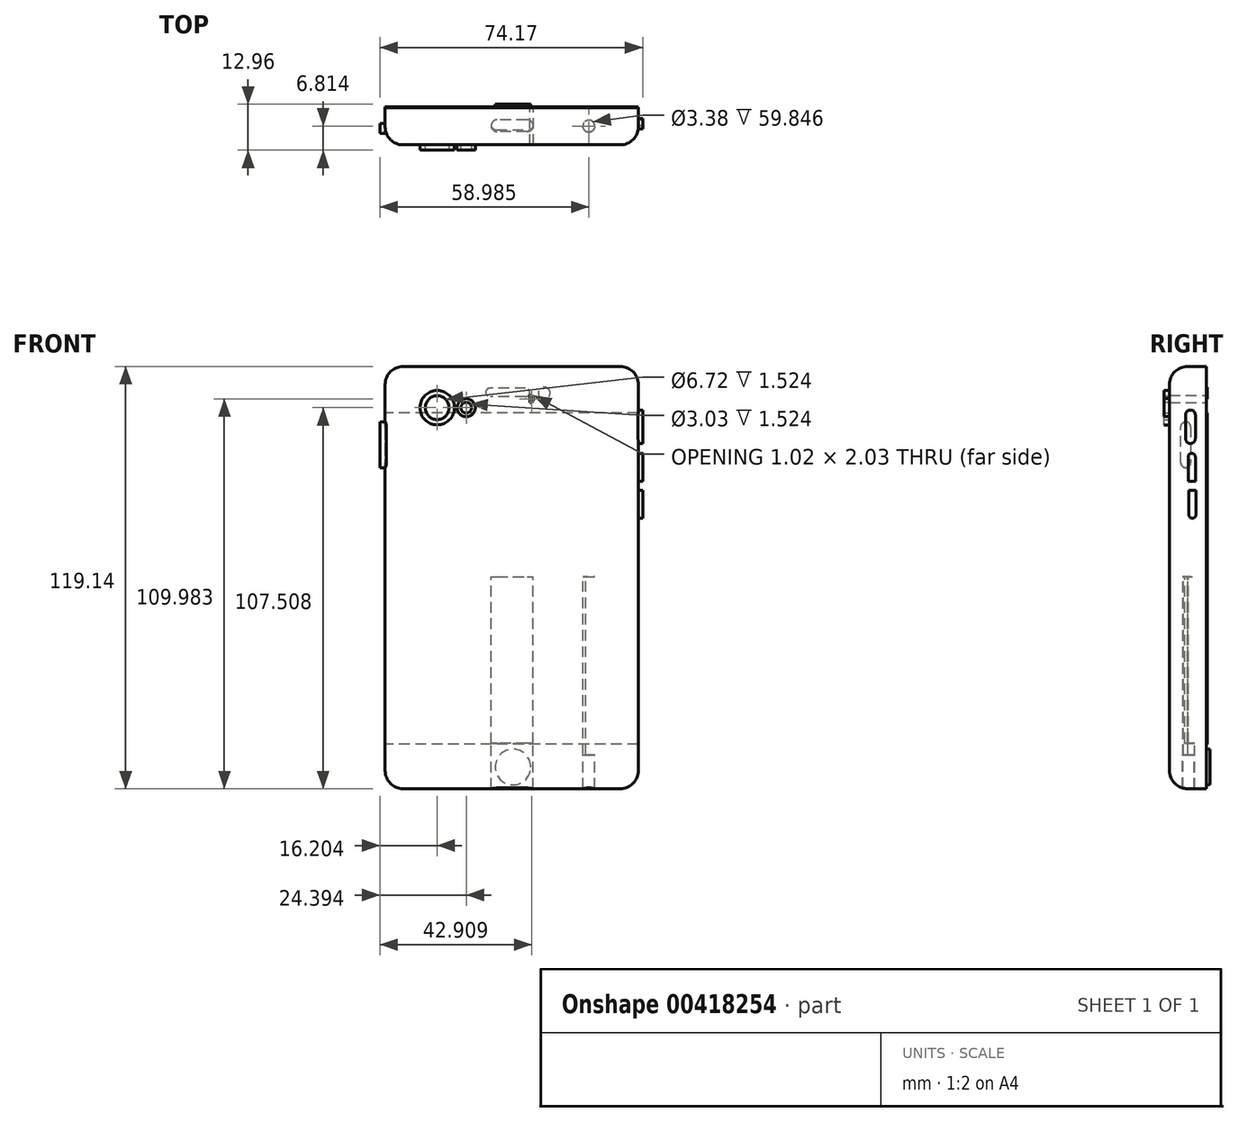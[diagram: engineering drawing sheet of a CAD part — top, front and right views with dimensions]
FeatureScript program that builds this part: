
annotation { "Feature Type Name" : "Feature", "Feature Type Description" : "" }
export const myFeature = defineFeature(function(context is Context, id is Id, definition is map)
    precondition{}
    {
        {
            var Q0;
            Q0=qCreatedBy(makeId("Front.planeOp"),FACE);
            var sketch = newSketch(context, id + "F0", { "sketchPlane" : qUnion([Q0])});
            skLineSegment(sketch, "E0.bottom", {"start": v(-32.74, 55.4) * mm, "end": v(31.45, 55.4) * mm});
            skLineSegment(sketch, "E0.top", {"start": v(-32.74, -55.78) * mm, "end": v(31.45, -55.78) * mm});
            skLineSegment(sketch, "E0.left", {"start": v(-32.74, 55.4) * mm, "end": v(-32.74, -55.78) * mm});
            skLineSegment(sketch, "E0.right", {"start": v(31.45, 55.4) * mm, "end": v(31.45, -55.78) * mm});
            skCircle(sketch, "E1", {"center": v(0, -48.2) * mm, "radius": 6.56 * mm});
            skLineSegment(sketch, "E2", {"start": v(-32.74, 43.75) * mm, "end": v(31.45, 43.75) * mm});
            skLineSegment(sketch, "E3.bottom", {"start": v(-4.25, 51.15) * mm, "end": v(4.8, 51.15) * mm});
            skLineSegment(sketch, "E3.top", {"start": v(-4.25, 49.12) * mm, "end": v(4.8, 49.12) * mm});
            skLineSegment(sketch, "E3.left", {"start": v(-4.25, 51.15) * mm, "end": v(-4.25, 49.12) * mm});
            skLineSegment(sketch, "E3.right", {"start": v(4.8, 51.15) * mm, "end": v(4.8, 49.12) * mm});
            skArc(sketch, "E4", {"start": v(4.8, 51.15) * mm, "mid": v(5.83, 50.13) * mm, "end": v(4.8, 49.12) * mm});
            skCircle(sketch, "E5", {"center": v(-8.7, 50.04) * mm, "radius": 1.1 * mm});
            skLineSegment(sketch, "E6.bottom", {"start": v(-36.07, 59.3) * mm, "end": v(35.33, 59.3) * mm});
            skLineSegment(sketch, "E6.top", {"start": v(-36.07, -59.85) * mm, "end": v(35.33, -59.85) * mm});
            skLineSegment(sketch, "E6.left", {"start": v(-36.07, 59.3) * mm, "end": v(-36.07, -59.85) * mm});
            skLineSegment(sketch, "E6.right", {"start": v(35.33, 59.3) * mm, "end": v(35.33, -59.85) * mm});
            skCircle(sketch, "E7", {"center": v(0, -48.2) * mm, "radius": 5.74 * mm});
            skCircle(sketch, "E8", {"center": v(-8.7, 50.04) * mm, "radius": 1.7 * mm});
            skSolve(sketch);
        }
        {
            var Q0;
            Q0 = qSketchRegion(id + "F0", true);
            var Q1;
            Q1=makeQuery(id+"F0.imprint","IMPRINT",FACE,{"disambiguationData":[TD([[makeQuery(id+"F0.imprint","IMPRINT",EDGE,{"derivedFrom":sQuery(id+"F0.wireOp",EDGE,"E7")}),1.0]])]});
            var Q2;
            Q2=makeQuery(id+"F0.imprint","IMPRINT",FACE,{"disambiguationData":[TD([[makeQuery(id+"F0.imprint","IMPRINT",EDGE,{"derivedFrom":sQuery(id+"F0.wireOp",EDGE,"E1")}),1.0]])]});
            var Q3;
            {var subQ1=sQuery(id+"F0.wireOp",EDGE,"E0.top");Q3=makeQuery(id+"F0.imprint","IMPRINT",FACE,{"disambiguationData":[TD([[makeQuery(id+"F0.imprint","IMPRINT",EDGE,{"derivedFrom":subQ1}),1.0]])]});}
            var Q4;
            Q4=makeQuery(id+"F0.imprint","IMPRINT",FACE,{"disambiguationData":[TD([[makeQuery(id+"F0.imprint","IMPRINT",EDGE,{"derivedFrom":sQuery(id+"F0.wireOp",EDGE,"E3.bottom")}),-1.0]])]});
            var Q5;
            Q5=makeQuery(id+"F0.imprint","IMPRINT",FACE,{"disambiguationData":[TD([[makeQuery(id+"F0.imprint","IMPRINT",EDGE,{"derivedFrom":sQuery(id+"F0.wireOp",EDGE,"E5")}),1.0]])]});
            var Q6;
            Q6=makeQuery(id+"F0.imprint","IMPRINT",FACE,{"disambiguationData":[TD([[makeQuery(id+"F0.imprint","IMPRINT",EDGE,{"derivedFrom":sQuery(id+"F0.wireOp",EDGE,"E4")}),-1.0]])]});
            var Q7;
            {var subQ1=sQuery(id+"F0.wireOp",EDGE,"E0.bottom");Q7=makeQuery(id+"F0.imprint","IMPRINT",FACE,{"disambiguationData":[TD([[makeQuery(id+"F0.imprint","IMPRINT",EDGE,{"derivedFrom":subQ1}),-1.0]])]});}
            var Q8;
            Q8=makeQuery(id+"F0.imprint","IMPRINT",FACE,{"disambiguationData":[TD([[makeQuery(id+"F0.imprint","IMPRINT",EDGE,{"derivedFrom":sQuery(id+"F0.wireOp",EDGE,"E5")}),-1.0]])]});
            extrude(context, id + "F1", {"entities" : qUnion([Q0, Q1, Q2, Q3, Q4, Q5, Q6, Q7, Q8]), "depth" : 10.4 * mm});
        }
        {
            var Q0;
            Q0=makeQuery(id+"F1.opExtrude","CAP_EDGE",EDGE,{"disambiguationData":[OSD([sQuery(id+"F0.wireOp",EDGE,"E6.bottom")])],"isStart":false});
            fillet(context, id + "F2", {"entities" : qUnion([Q0]), "radius" : 5.08 * mm, "tangentPropagation" : true, "allowEdgeOverflow" : false});
        }
        {
            var Q0;
            Q0=makeQuery(id+"F2.opFillet","BLEND_EDGE",EDGE,{"blendedFrom":[makeQuery(id+"F1.opExtrude","CAP_EDGE",EDGE,{"disambiguationData":[OSD([sQuery(id+"F0.wireOp",EDGE,"E6.bottom")])],"isStart":false}),makeQuery(id+"F1.opExtrude","SWEPT_FACE",FACE,{"disambiguationData":[OSD([sQuery(id+"F0.wireOp",EDGE,"E6.left")])]})],"blendedInto":[makeQuery(id+"F1.opExtrude","SWEPT_FACE",FACE,{"disambiguationData":[OSD([sQuery(id+"F0.wireOp",EDGE,"E6.left")])]})]});
            var Q1;
            Q1=makeQuery(id+"F2.opFillet","BLEND_EDGE",EDGE,{"blendedFrom":[makeQuery(id+"F1.opExtrude","CAP_EDGE",EDGE,{"disambiguationData":[OSD([sQuery(id+"F0.wireOp",EDGE,"E6.bottom")])],"isStart":false}),makeQuery(id+"F1.opExtrude","SWEPT_FACE",FACE,{"disambiguationData":[OSD([sQuery(id+"F0.wireOp",EDGE,"E6.right")])]})],"blendedInto":[makeQuery(id+"F1.opExtrude","SWEPT_FACE",FACE,{"disambiguationData":[OSD([sQuery(id+"F0.wireOp",EDGE,"E6.right")])]})]});
            var Q2;
            Q2=makeQuery(id+"F1.opExtrude","CAP_EDGE",EDGE,{"disambiguationData":[OSD([sQuery(id+"F0.wireOp",EDGE,"E6.left")])],"isStart":false});
            fillet(context, id + "F3", {"entities" : qUnion([Q0, Q1, Q2]), "radius" : 5.08 * mm, "tangentPropagation" : true, "allowEdgeOverflow" : false});
        }
        {
            var Q0;
            Q0=makeQuery(id+"F3.opFillet","BLEND_EDGE",EDGE,{"blendedFrom":[makeQuery(id+"F1.opExtrude","CAP_EDGE",EDGE,{"disambiguationData":[OSD([sQuery(id+"F0.wireOp",EDGE,"E6.left")])],"isStart":false}),makeQuery(id+"F1.opExtrude","SWEPT_FACE",FACE,{"disambiguationData":[OSD([sQuery(id+"F0.wireOp",EDGE,"E6.top")])]})],"blendedInto":[makeQuery(id+"F1.opExtrude","SWEPT_FACE",FACE,{"disambiguationData":[OSD([sQuery(id+"F0.wireOp",EDGE,"E6.top")])]})]});
            fillet(context, id + "F4", {"entities" : qUnion([Q0]), "radius" : 5.08 * mm, "tangentPropagation" : true, "allowEdgeOverflow" : false});
        }
        {
            var Q0;
            Q0=makeQuery(id+"F1.opExtrude","CAP_FACE",FACE,{"disambiguationData":[OSD([sQuery(id+"F0.wireOp",EDGE,"E6.bottom"),sQuery(id+"F0.wireOp",EDGE,"E6.top"),sQuery(id+"F0.wireOp",EDGE,"E6.left"),sQuery(id+"F0.wireOp",EDGE,"E6.right")])],"isStart":false});
            var sketch = newSketch(context, id + "F5", { "sketchPlane" : qUnion([Q0])});
            skCircle(sketch, "E9", {"center": v(-21.39, 47.66) * mm, "radius": 3.36 * mm});
            skCircle(sketch, "E10", {"center": v(-21.39, 47.66) * mm, "radius": 4.86 * mm});
            skCircle(sketch, "E11", {"center": v(-13.2, 47.66) * mm, "radius": 1.52 * mm});
            skCircle(sketch, "E12", {"center": v(-13.2, 47.66) * mm, "radius": 2.55 * mm});
            skSolve(sketch);
        }
        {
            var Q0;
            Q0=qCreatedBy(makeId("Right.planeOp"),FACE);
            var sketch = newSketch(context, id + "F6", { "sketchPlane" : qUnion([Q0])});
            skLineSegment(sketch, "E13.bottom", {"start": v(-5.92, 45.6) * mm, "end": v(-3.14, 45.6) * mm});
            skLineSegment(sketch, "E13.top", {"start": v(-5.92, 38.94) * mm, "end": v(-3.14, 38.94) * mm});
            skLineSegment(sketch, "E13.left", {"start": v(-5.92, 45.6) * mm, "end": v(-5.92, 38.94) * mm});
            skLineSegment(sketch, "E13.right", {"start": v(-3.14, 45.6) * mm, "end": v(-3.14, 38.94) * mm});
            skLineSegment(sketch, "E14.bottom", {"start": v(-5.18, 33.76) * mm, "end": v(-3.14, 33.76) * mm});
            skLineSegment(sketch, "E14.top", {"start": v(-5.18, 26.92) * mm, "end": v(-3.14, 26.92) * mm});
            skLineSegment(sketch, "E14.left", {"start": v(-5.18, 33.76) * mm, "end": v(-5.18, 26.92) * mm});
            skLineSegment(sketch, "E14.right", {"start": v(-3.14, 33.76) * mm, "end": v(-3.14, 26.92) * mm});
            skLineSegment(sketch, "E15.bottom", {"start": v(-5, 24.33) * mm, "end": v(-2.96, 24.33) * mm});
            skLineSegment(sketch, "E15.top", {"start": v(-5, 17.48) * mm, "end": v(-2.96, 17.48) * mm});
            skLineSegment(sketch, "E15.left", {"start": v(-5, 24.33) * mm, "end": v(-5, 17.48) * mm});
            skLineSegment(sketch, "E15.right", {"start": v(-2.96, 24.33) * mm, "end": v(-2.96, 17.48) * mm});
            skArc(sketch, "E16", {"start": v(-5.92, 45.6) * mm, "mid": v(-4.53, 46.99) * mm, "end": v(-3.14, 45.6) * mm});
            skArc(sketch, "E17", {"start": v(-5.92, 38.94) * mm, "mid": v(-4.53, 37.55) * mm, "end": v(-3.14, 38.94) * mm});
            skArc(sketch, "E18", {"start": v(-5.18, 33.76) * mm, "mid": v(-4.16, 34.78) * mm, "end": v(-3.14, 33.76) * mm});
            skArc(sketch, "E19", {"start": v(-5, 17.48) * mm, "mid": v(-3.98, 16.46) * mm, "end": v(-2.96, 17.48) * mm});
            skSolve(sketch);
        }
        {
            var Q0;
            Q0 = qSketchRegion(id + "F6", true);
            extrude(context, id + "F7", {"entities" : qUnion([Q0]), "operationType" : NewBodyOperationType.ADD, "depth" : 36.58 * mm});
        }
        {
            var Q0;
            Q0=qCreatedBy(makeId("Right.planeOp"),FACE);
            var sketch = newSketch(context, id + "F8", { "sketchPlane" : qUnion([Q0])});
            skLineSegment(sketch, "E20.bottom", {"start": v(-4.44, 42.27) * mm, "end": v(-7.21, 42.27) * mm});
            skLineSegment(sketch, "E20.top", {"start": v(-4.44, 32.1) * mm, "end": v(-7.21, 32.1) * mm});
            skLineSegment(sketch, "E20.left", {"start": v(-4.44, 42.27) * mm, "end": v(-4.44, 32.1) * mm});
            skLineSegment(sketch, "E20.right", {"start": v(-7.21, 42.27) * mm, "end": v(-7.21, 32.1) * mm});
            skArc(sketch, "E21", {"start": v(-7.21, 32.1) * mm, "mid": v(-5.83, 30.7) * mm, "end": v(-4.44, 32.1) * mm});
            skArc(sketch, "E22", {"start": v(-4.44, 42.27) * mm, "mid": v(-5.83, 43.66) * mm, "end": v(-7.21, 42.27) * mm});
            skSolve(sketch);
        }
        {
            var Q0;
            Q0 = qSketchRegion(id + "F8", true);
            extrude(context, id + "F9", {"entities" : qUnion([Q0]), "operationType" : NewBodyOperationType.ADD, "oppositeDirection" : true, "depth" : 37.6 * mm});
        }
        {
            var Q0;
            Q0 = qSketchRegion(id + "F5", true);
            extrude(context, id + "F10", {"entities" : qUnion([Q0]), "operationType" : NewBodyOperationType.ADD, "depth" : 1.52 * mm});
        }
        {
            var Q0;
            Q0=qCreatedBy(makeId("Front.planeOp"),FACE);
            var sketch = newSketch(context, id + "F11", { "sketchPlane" : qUnion([Q0])});
            skCircle(sketch, "E23", {"center": v(0, -53.74) * mm, "radius": 5.03 * mm});
            skSolve(sketch);
        }
        {
            var Q0;
            Q0 = qSketchRegion(id + "F11", true);
            extrude(context, id + "F12", {"entities" : qUnion([Q0]), "operationType" : NewBodyOperationType.ADD, "oppositeDirection" : true, "depth" : 1.02 * mm});
        }
        {
            var Q0;
            Q0=qCreatedBy(makeId("Front.planeOp"),FACE);
            var sketch = newSketch(context, id + "F13", { "sketchPlane" : qUnion([Q0])});
            skLineSegment(sketch, "E24.bottom", {"start": v(35.27, 46.19) * mm, "end": v(-36.07, 46.19) * mm});
            skLineSegment(sketch, "E24.top", {"start": v(35.27, -47.25) * mm, "end": v(-36.07, -47.25) * mm});
            skLineSegment(sketch, "E24.left", {"start": v(35.27, 46.19) * mm, "end": v(35.27, -47.25) * mm});
            skLineSegment(sketch, "E24.right", {"start": v(-36.07, 46.19) * mm, "end": v(-36.07, -47.25) * mm});
            skSolve(sketch);
        }
        {
            var Q0;
            Q0 = qSketchRegion(id + "F13", true);
            extrude(context, id + "F14", {"entities" : qUnion([Q0]), "operationType" : NewBodyOperationType.ADD, "oppositeDirection" : true, "depth" : 0.25 * mm});
        }
        {
            var Q0;
            Q0=qCreatedBy(makeId("Front.planeOp"),FACE);
            var sketch = newSketch(context, id + "F15", { "sketchPlane" : qUnion([Q0])});
            skLineSegment(sketch, "E25.bottom", {"start": v(3.51, 53.19) * mm, "end": v(-6.47, 53.19) * mm});
            skLineSegment(sketch, "E25.top", {"start": v(3.51, 50.78) * mm, "end": v(-6.47, 50.78) * mm});
            skLineSegment(sketch, "E25.left", {"start": v(3.51, 53.19) * mm, "end": v(3.51, 50.78) * mm});
            skLineSegment(sketch, "E25.right", {"start": v(-6.47, 53.19) * mm, "end": v(-6.47, 50.78) * mm});
            skArc(sketch, "E26", {"start": v(3.51, 50.78) * mm, "mid": v(4.72, 51.98) * mm, "end": v(3.51, 53.19) * mm});
            skArc(sketch, "E27", {"start": v(-6.47, 53.19) * mm, "mid": v(-7.68, 51.98) * mm, "end": v(-6.47, 50.78) * mm});
            skSolve(sketch);
        }
        {
            var Q0;
            Q0 = qSketchRegion(id + "F15", true);
            extrude(context, id + "F16", {"entities" : qUnion([Q0]), "operationType" : NewBodyOperationType.ADD, "oppositeDirection" : true, "depth" : 0.25 * mm});
        }
        {
            var Q0;
            Q0=qCreatedBy(makeId("Front.planeOp"),FACE);
            var sketch = newSketch(context, id + "F17", { "sketchPlane" : qUnion([Q0])});
            skCircle(sketch, "E28", {"center": v(8.81, 51.8) * mm, "radius": 1.66 * mm});
            skSolve(sketch);
        }
        {
            var Q0;
            Q0 = qSketchRegion(id + "F17", true);
            extrude(context, id + "F18", {"entities" : qUnion([Q0]), "operationType" : NewBodyOperationType.ADD, "oppositeDirection" : true, "depth" : 0.25 * mm});
        }
        {
            var Q0;
            Q0=qCreatedBy(makeId("Top.planeOp"),FACE);
            var sketch = newSketch(context, id + "F19", { "sketchPlane" : qUnion([Q0])});
            skLineSegment(sketch, "E29.bottom", {"start": v(-4.46, -6.69) * mm, "end": v(4.01, -6.69) * mm});
            skLineSegment(sketch, "E29.top", {"start": v(-4.46, -3.34) * mm, "end": v(4.01, -3.34) * mm});
            skLineSegment(sketch, "E29.left", {"start": v(-4.46, -6.69) * mm, "end": v(-4.46, -3.34) * mm});
            skLineSegment(sketch, "E29.right", {"start": v(4.01, -6.69) * mm, "end": v(4.01, -3.34) * mm});
            skArc(sketch, "E30", {"start": v(4.01, -6.69) * mm, "mid": v(5.68, -5.01) * mm, "end": v(4.01, -3.34) * mm});
            skArc(sketch, "E31", {"start": v(-4.46, -3.34) * mm, "mid": v(-6.13, -5.01) * mm, "end": v(-4.46, -6.69) * mm});
            skSolve(sketch);
        }
        {
            var Q0;
            Q0 = qSketchRegion(id + "F19", true);
            extrude(context, id + "F20", {"entities" : qUnion([Q0]), "operationType" : NewBodyOperationType.REMOVE, "oppositeDirection" : true, "depth" : 69.85 * mm});
        }
        {
            var Q0;
            Q0=qCreatedBy(makeId("Top.planeOp"),FACE);
            var sketch = newSketch(context, id + "F21", { "sketchPlane" : qUnion([Q0])});
            skLineSegment(sketch, "E32.bottom", {"start": v(-4.72, -6.16) * mm, "end": v(4.32, -6.16) * mm});
            skLineSegment(sketch, "E32.top", {"start": v(-4.72, -3.18) * mm, "end": v(4.32, -3.18) * mm});
            skLineSegment(sketch, "E32.left", {"start": v(-4.72, -6.16) * mm, "end": v(-4.72, -3.18) * mm});
            skLineSegment(sketch, "E32.right", {"start": v(4.32, -6.16) * mm, "end": v(4.32, -3.18) * mm});
            skArc(sketch, "E33", {"start": v(4.32, -6.16) * mm, "mid": v(5.82, -4.67) * mm, "end": v(4.32, -3.18) * mm});
            skArc(sketch, "E34", {"start": v(-4.72, -3.18) * mm, "mid": v(-6.2, -4.67) * mm, "end": v(-4.72, -6.16) * mm});
            skSolve(sketch);
        }
        {
            var Q0;
            Q0 = qSketchRegion(id + "F21", true);
            extrude(context, id + "F22", {"entities" : qUnion([Q0]), "operationType" : NewBodyOperationType.ADD, "oppositeDirection" : true, "depth" : 47 * mm});
        }
        {
            var Q0;
            Q0=qCreatedBy(makeId("Top.planeOp"),FACE);
            var sketch = newSketch(context, id + "F23", { "sketchPlane" : qUnion([Q0])});
            skCircle(sketch, "E35", {"center": v(21.4, -5.13) * mm, "radius": 1.69 * mm});
            skSolve(sketch);
        }
        {
            var Q0;
            Q0 = qSketchRegion(id + "F23", true);
            extrude(context, id + "F24", {"entities" : qUnion([Q0]), "operationType" : NewBodyOperationType.REMOVE, "oppositeDirection" : true, "depth" : 77.22 * mm});
        }
        {
            var Q0;
            Q0=qCreatedBy(makeId("Top.planeOp"),FACE);
            var sketch = newSketch(context, id + "F25", { "sketchPlane" : qUnion([Q0])});
            skCircle(sketch, "E36", {"center": v(11.65, -5.09) * mm, "radius": 1.7 * mm});
            skCircle(sketch, "E37", {"center": v(16.83, -5.09) * mm, "radius": 2.07 * mm});
            skCircle(sketch, "E38", {"center": v(21.46, -5.09) * mm, "radius": 1.76 * mm});
            skCircle(sketch, "E39", {"center": v(26.08, -5.09) * mm, "radius": 2 * mm});
            skSolve(sketch);
        }
        {
            var Q0;
            Q0 = qSketchRegion(id + "F25", true);
            extrude(context, id + "F26", {"entities" : qUnion([Q0]), "operationType" : NewBodyOperationType.ADD, "oppositeDirection" : true, "depth" : 50.3 * mm});
        }
    });
